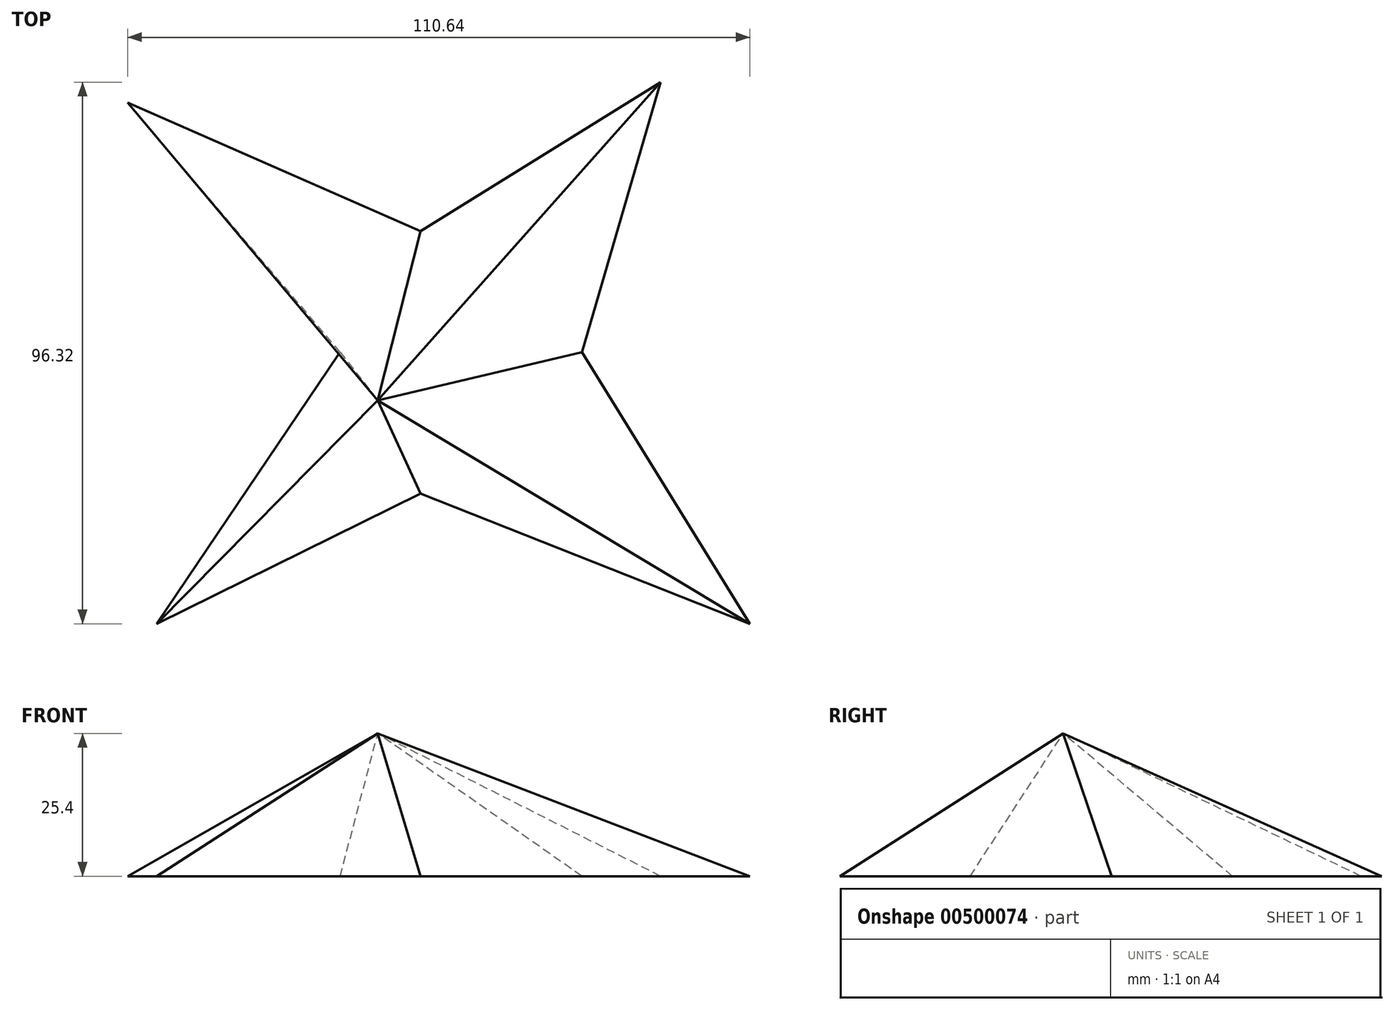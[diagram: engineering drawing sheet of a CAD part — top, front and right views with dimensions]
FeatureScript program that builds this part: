
annotation { "Feature Type Name" : "Feature", "Feature Type Description" : "" }
export const myFeature = defineFeature(function(context is Context, id is Id, definition is map)
    precondition{}
    {
        {
            var Q0;
            Q0=qCreatedBy(makeId("Top.planeOp"),FACE);
            var sketch = newSketch(context, id + "F0", { "sketchPlane" : qUnion([Q0])});
            skLineSegment(sketch, "E0", {"start": v(0, 21.49) * mm, "end": v(42.67, 48) * mm});
            skLineSegment(sketch, "E1", {"start": v(42.67, 48) * mm, "end": v(28.65, 0) * mm});
            skLineSegment(sketch, "E2", {"start": v(28.65, 0) * mm, "end": v(58.52, -48.31) * mm});
            skLineSegment(sketch, "E3", {"start": v(58.52, -48.31) * mm, "end": v(0, -25.15) * mm});
            skLineSegment(sketch, "E4", {"start": v(0, -25.15) * mm, "end": v(-46.94, -48.31) * mm});
            skLineSegment(sketch, "E5", {"start": v(-46.94, -48.31) * mm, "end": v(-14.33, 0) * mm});
            skLineSegment(sketch, "E6", {"start": v(-14.33, 0) * mm, "end": v(-52.12, 44.35) * mm});
            skLineSegment(sketch, "E7", {"start": v(-52.12, 44.35) * mm, "end": v(0, 21.49) * mm});
            skSolve(sketch);
        }
        {
            var Q0;
            Q0=qCreatedBy(makeId("Top.planeOp"),FACE);
            cPlane(context, id + "F1", {"entities" : qUnion([Q0]), "cplaneType" : CPlaneType.OFFSET, "offset" : 25.4 * mm, "width" : 152.4 * mm, "height" : 152.4 * mm});
        }
        {
            var Q0;
            Q0=qCreatedBy(id+"F1.planeOp",FACE);
            var sketch = newSketch(context, id + "F2", { "sketchPlane" : qUnion([Q0])});
            skPoint(sketch, "E8", {"position": v(-7.62, -8.6) * mm});
            skSolve(sketch);
        }
        {
            var Q0;
            Q0=makeQuery(id+"F0.imprint","IMPRINT",FACE,{"disambiguationData":[TD([[makeQuery(id+"F0.imprint","IMPRINT",EDGE,{"derivedFrom":sQuery(id+"F0.wireOp",EDGE,"E0")}),-1.0]])]});
            var Q1;
            Q1=sQuery(id+"F2.wireOp",VERTEX,"E8");
            loft(context, id + "F3", {"sheetProfilesArray" : [{ "sheetProfileEntities" : qUnion([Q0]) }, { "sheetProfileEntities" : qUnion([Q1]) }]});
        }
    });
